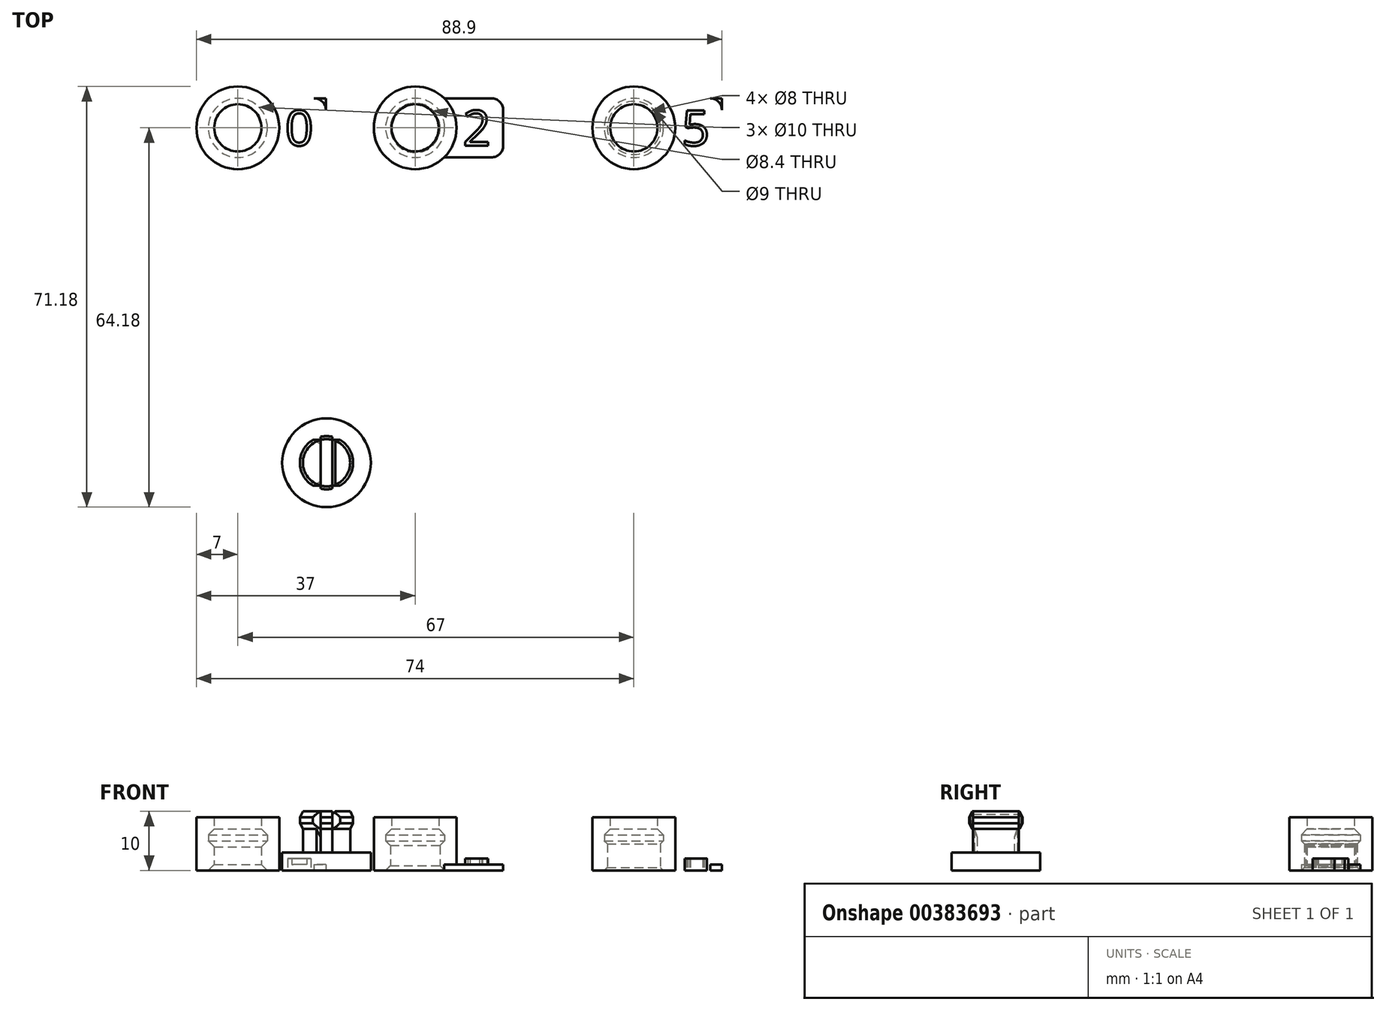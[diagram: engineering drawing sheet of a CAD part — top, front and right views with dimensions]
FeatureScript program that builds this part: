
annotation { "Feature Type Name" : "Feature", "Feature Type Description" : "" }
export const myFeature = defineFeature(function(context is Context, id is Id, definition is map)
    precondition{}
    {
        {
            var Q0;
            Q0=qCreatedBy(makeId("Front.planeOp"),FACE);
            var sketch = newSketch(context, id + "F0", { "sketchPlane" : qUnion([Q0])});
            skLineSegment(sketch, "E0", {"start": v(0, 0) * mm, "end": v(0, 7) * mm, "construction": true});
            skLineSegment(sketch, "E1", {"start": v(0, 7) * mm, "end": v(0, 9) * mm, "construction": true});
            skLineSegment(sketch, "E2", {"start": v(0, 9) * mm, "end": v(-4, 9) * mm, "construction": true});
            skLineSegment(sketch, "E3", {"start": v(0, 0) * mm, "end": v(-4, 0) * mm, "construction": true});
            skLineSegment(sketch, "E4", {"start": v(-4, 9) * mm, "end": v(-4, 7) * mm});
            skLineSegment(sketch, "E5", {"start": v(-4, 7) * mm, "end": v(-5, 6) * mm});
            skLineSegment(sketch, "E6", {"start": v(-5, 6) * mm, "end": v(-5, 5) * mm});
            skLineSegment(sketch, "E7", {"start": v(-5, 5) * mm, "end": v(-4, 4) * mm});
            skLineSegment(sketch, "E8", {"start": v(-4, 4) * mm, "end": v(-4, 0) * mm});
            skLineSegment(sketch, "E9", {"start": v(-4, 0) * mm, "end": v(-7, 0) * mm});
            skLineSegment(sketch, "E10", {"start": v(-7, 0) * mm, "end": v(-7, 9) * mm});
            skLineSegment(sketch, "E11", {"start": v(-7, 9) * mm, "end": v(-4, 9) * mm});
            skLineSegment(sketch, "E12", {"start": v(-4, 1) * mm, "end": v(-5, 0) * mm});
            skLineSegment(sketch, "E13", {"start": v(30, 0) * mm, "end": v(30, 7) * mm, "construction": true});
            skLineSegment(sketch, "E14", {"start": v(30, 7) * mm, "end": v(30, 9) * mm, "construction": true});
            skLineSegment(sketch, "E15", {"start": v(30, 9) * mm, "end": v(26, 9) * mm, "construction": true});
            skLineSegment(sketch, "E16", {"start": v(30, 0) * mm, "end": v(25.8, 0) * mm, "construction": true});
            skLineSegment(sketch, "E17", {"start": v(26, 9) * mm, "end": v(26, 7) * mm});
            skLineSegment(sketch, "E18", {"start": v(26, 7) * mm, "end": v(25, 6) * mm});
            skLineSegment(sketch, "E19", {"start": v(25, 6) * mm, "end": v(25, 5) * mm});
            skLineSegment(sketch, "E20", {"start": v(25, 5) * mm, "end": v(25.8, 4.2) * mm});
            skLineSegment(sketch, "E21", {"start": v(25.8, 4.2) * mm, "end": v(25.8, 0) * mm});
            skLineSegment(sketch, "E22", {"start": v(25.8, 0) * mm, "end": v(23, 0) * mm});
            skLineSegment(sketch, "E23", {"start": v(23, 0) * mm, "end": v(23, 9) * mm});
            skLineSegment(sketch, "E24", {"start": v(23, 9) * mm, "end": v(26, 9) * mm});
            skLineSegment(sketch, "E25", {"start": v(25.8, 0.8) * mm, "end": v(25, 0) * mm});
            skLineSegment(sketch, "E26", {"start": v(67, 0) * mm, "end": v(67, 7) * mm, "construction": true});
            skLineSegment(sketch, "E27", {"start": v(67, 7) * mm, "end": v(67, 9) * mm, "construction": true});
            skLineSegment(sketch, "E28", {"start": v(67, 9) * mm, "end": v(63, 9) * mm, "construction": true});
            skLineSegment(sketch, "E29", {"start": v(67, 0) * mm, "end": v(62.5, 0) * mm, "construction": true});
            skLineSegment(sketch, "E30", {"start": v(63, 9) * mm, "end": v(63, 7) * mm});
            skLineSegment(sketch, "E31", {"start": v(63, 7) * mm, "end": v(62, 6) * mm});
            skLineSegment(sketch, "E32", {"start": v(62, 6) * mm, "end": v(62, 5) * mm});
            skLineSegment(sketch, "E33", {"start": v(62, 5) * mm, "end": v(62.5, 4.5) * mm});
            skLineSegment(sketch, "E34", {"start": v(62.5, 4.5) * mm, "end": v(62.5, 0) * mm});
            skLineSegment(sketch, "E35", {"start": v(62.5, 0) * mm, "end": v(60, 0) * mm});
            skLineSegment(sketch, "E36", {"start": v(60, 0) * mm, "end": v(60, 9) * mm});
            skLineSegment(sketch, "E37", {"start": v(60, 9) * mm, "end": v(63, 9) * mm});
            skLineSegment(sketch, "E38", {"start": v(62.5, 0.5) * mm, "end": v(62, 0) * mm});
            skSolve(sketch);
        }
        {
            var Q0;
            Q0=makeQuery(id+"F0.imprint","IMPRINT",FACE,{"disambiguationData":[TD([[makeQuery(id+"F0.imprint","IMPRINT",EDGE,{"derivedFrom":sQuery(id+"F0.wireOp",EDGE,"E4")}),-1.0]])]});
            var Q1;
            Q1=sQuery(id+"F0.wireOp",EDGE,"E0");
            revolve(context, id + "F1", {"entities" : qUnion([Q0]), "axis" : qUnion([Q1]), "revolveType" : RevolveType.FULL});
        }
        {
            var Q0;
            Q0=makeQuery(id+"F0.imprint","IMPRINT",FACE,{"disambiguationData":[TD([[makeQuery(id+"F0.imprint","IMPRINT",EDGE,{"derivedFrom":sQuery(id+"F0.wireOp",EDGE,"E17")}),-1.0]])]});
            var Q1;
            Q1=sQuery(id+"F0.wireOp",EDGE,"E13");
            revolve(context, id + "F2", {"entities" : qUnion([Q0]), "axis" : qUnion([Q1]), "revolveType" : RevolveType.FULL});
        }
        {
            var Q0;
            Q0=makeQuery(id+"F0.imprint","IMPRINT",FACE,{"disambiguationData":[TD([[makeQuery(id+"F0.imprint","IMPRINT",EDGE,{"derivedFrom":sQuery(id+"F0.wireOp",EDGE,"E30")}),-1.0]])]});
            var Q1;
            Q1=sQuery(id+"F0.wireOp",EDGE,"E26");
            revolve(context, id + "F3", {"entities" : qUnion([Q0]), "axis" : qUnion([Q1]), "revolveType" : RevolveType.FULL});
        }
        {
            var Q0;
            Q0=qCreatedBy(makeId("Top.planeOp"),FACE);
            var sketch = newSketch(context, id + "F4", { "sketchPlane" : qUnion([Q0])});
            skCircle(sketch, "E39.0", {"center": v(0, 0) * mm, "radius": 7 * mm});
            skCircle(sketch, "E40.0", {"center": v(30, 0) * mm, "radius": 7 * mm});
            skCircle(sketch, "E41.0", {"center": v(67, 0) * mm, "radius": 7 * mm});
            skLineSegment(sketch, "E42.bottom", {"start": v(4.9, 5) * mm, "end": v(14.9, 5) * mm});
            skLineSegment(sketch, "E42.top", {"start": v(4.9, -5) * mm, "end": v(14.9, -5) * mm});
            skLineSegment(sketch, "E42.left", {"start": v(4.9, 5) * mm, "end": v(4.9, -5) * mm, "construction": true});
            skLineSegment(sketch, "E42.right", {"start": v(14.9, 5) * mm, "end": v(14.9, -5) * mm});
            skLineSegment(sketch, "E43", {"start": v(0, 0) * mm, "end": v(67, 0) * mm, "construction": true});
            skLineSegment(sketch, "E44.bottom", {"start": v(34.9, 5) * mm, "end": v(44.9, 5) * mm});
            skLineSegment(sketch, "E44.top", {"start": v(34.9, -5) * mm, "end": v(44.9, -5) * mm});
            skLineSegment(sketch, "E44.left", {"start": v(34.9, 5) * mm, "end": v(34.9, -5) * mm, "construction": true});
            skLineSegment(sketch, "E44.right", {"start": v(44.9, 5) * mm, "end": v(44.9, -5) * mm});
            skLineSegment(sketch, "E45.bottom", {"start": v(71.9, 5) * mm, "end": v(81.9, 5) * mm});
            skLineSegment(sketch, "E45.top", {"start": v(71.9, -5) * mm, "end": v(81.9, -5) * mm});
            skLineSegment(sketch, "E45.left", {"start": v(71.9, 5) * mm, "end": v(71.9, -5) * mm, "construction": true});
            skLineSegment(sketch, "E45.right", {"start": v(81.9, 5) * mm, "end": v(81.9, -5) * mm});
            skArc(sketch, "E46", {"start": v(12.9, 5) * mm, "mid": v(14.31, 4.41) * mm, "end": v(14.9, 3) * mm});
            skArc(sketch, "E47", {"start": v(14.9, -3) * mm, "mid": v(14.31, -4.41) * mm, "end": v(12.9, -5) * mm});
            skArc(sketch, "E48", {"start": v(42.9, -5) * mm, "mid": v(44.31, -4.41) * mm, "end": v(44.9, -3) * mm});
            skArc(sketch, "E49", {"start": v(42.9, 5) * mm, "mid": v(44.31, 4.41) * mm, "end": v(44.9, 3) * mm});
            skArc(sketch, "E50", {"start": v(79.9, 5) * mm, "mid": v(81.31, 4.41) * mm, "end": v(81.9, 3) * mm});
            skArc(sketch, "E51", {"start": v(81.9, -3) * mm, "mid": v(81.31, -4.41) * mm, "end": v(79.9, -5) * mm});
            skText(sketch, "E52", { "text": "0", "fontName": "OpenSans-Regular.ttf"});
            skText(sketch, "E53", { "text": "2", "fontName": "OpenSans-Regular.ttf"});
            skText(sketch, "E54", { "text": "5", "fontName": "OpenSans-Regular.ttf"});
            const initialGuessF4  = {"E52": [0.008, -0.003, 1, 0, 0.006], "E53": [0.03804, -0.003, 1, 0, 0.006], "E54": [0.07507, -0.003, 1, 0, 0.006]};
            skSetInitialGuess(sketch, initialGuessF4);
            skSolve(sketch);
        }
        {
            var Q0;
            {var subQ6=sQuery(id+"F4.wireOp",EDGE,"E46");Q0=makeQuery(id+"F4.imprint","IMPRINT",FACE,{"disambiguationData":[TD([[makeQuery(id+"F4.imprint","IMPRINT",EDGE,{"derivedFrom":subQ6}),-1.0]])]});}
            var Q1;
            Q1=makeQuery(id+"F4.imprint","IMPRINT",FACE,{"disambiguationData":[TD([[makeQuery(id+"F4.imprint","IMPRINT",EDGE,{"derivedFrom":sQuery(id+"F4.wireOp",EDGE,"E52.sketch_text.stroke-0")}),-1.0]])]});
            var Q2;
            Q2=makeQuery(id+"F4.imprint","IMPRINT",FACE,{"disambiguationData":[TD([[makeQuery(id+"F4.imprint","IMPRINT",EDGE,{"derivedFrom":sQuery(id+"F4.wireOp",EDGE,"E52.sketch_text.stroke-8")}),1.0]])]});
            extrude(context, id + "F5", {"entities" : qUnion([Q0, Q1, Q2]), "operationType" : NewBodyOperationType.ADD, "depth" : 1 * mm});
        }
        {
            var Q0;
            {var subQ3=sQuery(id+"F4.wireOp",EDGE,"E48");Q0=makeQuery(id+"F4.imprint","IMPRINT",FACE,{"disambiguationData":[TD([[makeQuery(id+"F4.imprint","IMPRINT",EDGE,{"derivedFrom":subQ3}),1.0]])]});}
            var Q1;
            Q1=makeQuery(id+"F4.imprint","IMPRINT",FACE,{"disambiguationData":[TD([[makeQuery(id+"F4.imprint","IMPRINT",EDGE,{"derivedFrom":sQuery(id+"F4.wireOp",EDGE,"E53.sketch_text.stroke-0")}),-1.0]])]});
            extrude(context, id + "F6", {"entities" : qUnion([Q0, Q1]), "operationType" : NewBodyOperationType.ADD, "depth" : 1 * mm});
        }
        {
            var Q0;
            {var subQ0=sQuery(id+"F4.wireOp",EDGE,"E50");Q0=makeQuery(id+"F4.imprint","IMPRINT",FACE,{"disambiguationData":[TD([[makeQuery(id+"F4.imprint","IMPRINT",EDGE,{"derivedFrom":subQ0}),-1.0]])]});}
            var Q1;
            Q1=makeQuery(id+"F4.imprint","IMPRINT",FACE,{"disambiguationData":[TD([[makeQuery(id+"F4.imprint","IMPRINT",EDGE,{"derivedFrom":sQuery(id+"F4.wireOp",EDGE,"E54.sketch_text.stroke-0")}),-1.0]])]});
            extrude(context, id + "F7", {"entities" : qUnion([Q0, Q1]), "operationType" : NewBodyOperationType.ADD, "depth" : 1 * mm});
        }
        {
            var Q0;
            Q0=makeQuery(id+"F4.imprint","IMPRINT",FACE,{"disambiguationData":[TD([[makeQuery(id+"F4.imprint","IMPRINT",EDGE,{"derivedFrom":sQuery(id+"F4.wireOp",EDGE,"E52.sketch_text.stroke-0")}),-1.0]])]});
            extrude(context, id + "F8", {"entities" : qUnion([Q0]), "operationType" : NewBodyOperationType.ADD, "depth" : 2 * mm});
        }
        {
            var Q0;
            Q0=makeQuery(id+"F4.imprint","IMPRINT",FACE,{"disambiguationData":[TD([[makeQuery(id+"F4.imprint","IMPRINT",EDGE,{"derivedFrom":sQuery(id+"F4.wireOp",EDGE,"E53.sketch_text.stroke-0")}),-1.0]])]});
            extrude(context, id + "F9", {"entities" : qUnion([Q0]), "operationType" : NewBodyOperationType.ADD, "depth" : 2 * mm});
        }
        {
            var Q0;
            Q0=makeQuery(id+"F4.imprint","IMPRINT",FACE,{"disambiguationData":[TD([[makeQuery(id+"F4.imprint","IMPRINT",EDGE,{"derivedFrom":sQuery(id+"F4.wireOp",EDGE,"E54.sketch_text.stroke-0")}),-1.0]])]});
            extrude(context, id + "F10", {"entities" : qUnion([Q0]), "operationType" : NewBodyOperationType.ADD, "depth" : 2 * mm});
        }
        {
            var Q0;
            Q0=qCreatedBy(makeId("Top.planeOp"),FACE);
            var sketch = newSketch(context, id + "F11", { "sketchPlane" : qUnion([Q0])});
            skLineSegment(sketch, "E55", {"start": v(0, -30.7) * mm, "end": v(30, -30.7) * mm, "construction": true});
            skLineSegment(sketch, "E56", {"start": v(30, -30.7) * mm, "end": v(15, -56.68) * mm, "construction": true});
            skLineSegment(sketch, "E57", {"start": v(15, -56.68) * mm, "end": v(0, -30.7) * mm, "construction": true});
            skLineSegment(sketch, "E58", {"start": v(0, -56.68) * mm, "end": v(30, -56.68) * mm, "construction": true});
            skLineSegment(sketch, "E59", {"start": v(15, -30.7) * mm, "end": v(15, -82.66) * mm, "construction": true});
            skSolve(sketch);
        }
        {
            var Q0;
            Q0=sQuery(id+"F11.wireOp",EDGE,"E58");
            cPoint(context, id + "F12", {"entities" : qUnion([Q0]), "parameter" : 0.5});
        }
        {
            var Q0;
            Q0=qCreatedBy(id+"F12",VERTEX);
            var Q1;
            Q1=sQuery(id+"F11.wireOp",EDGE,"E58");
            cPlane(context, id + "F13", {"entities" : qUnion([Q0, Q1]), "cplaneType" : CPlaneType.LINE_POINT, "offset" : 25 * mm, "width" : 150 * mm, "height" : 150 * mm});
        }
        {
            var Q0;
            Q0=qCreatedBy(id+"F13.planeOp",FACE);
            var sketch = newSketch(context, id + "F14", { "sketchPlane" : qUnion([Q0])});
            skPoint(sketch, "E60.0", {"position": v(-56.68, 0) * mm});
            skLineSegment(sketch, "E61", {"start": v(-56.68, 0) * mm, "end": v(-56.68, 10) * mm});
            skLineSegment(sketch, "E62", {"start": v(-56.68, 10) * mm, "end": v(-52.68, 10) * mm});
            skLineSegment(sketch, "E63", {"start": v(-52.68, 10) * mm, "end": v(-52.18, 9) * mm});
            skLineSegment(sketch, "E64", {"start": v(-52.18, 9) * mm, "end": v(-52.18, 8) * mm});
            skLineSegment(sketch, "E65", {"start": v(-52.18, 8) * mm, "end": v(-52.68, 7) * mm});
            skLineSegment(sketch, "E66", {"start": v(-52.68, 7) * mm, "end": v(-52.68, 0) * mm});
            skLineSegment(sketch, "E67", {"start": v(-52.68, 0) * mm, "end": v(-56.68, 0) * mm});
            skLineSegment(sketch, "E68", {"start": v(-52.68, 0) * mm, "end": v(-49.18, 0) * mm});
            skLineSegment(sketch, "E69", {"start": v(-49.18, 0) * mm, "end": v(-49.18, 3) * mm});
            skLineSegment(sketch, "E70", {"start": v(-49.18, 3) * mm, "end": v(-52.68, 3) * mm});
            skSolve(sketch);
        }
        {
            var Q0;
            {var subQ0=sQuery(id+"F14.wireOp",EDGE,"E68");Q0=makeQuery(id+"F14.imprint","IMPRINT",FACE,{"disambiguationData":[TD([[makeQuery(id+"F14.imprint","IMPRINT",EDGE,{"derivedFrom":subQ0}),1.0]])]});}
            var Q1;
            Q1=makeQuery(id+"F14.imprint","IMPRINT",FACE,{"disambiguationData":[TD([[makeQuery(id+"F14.imprint","IMPRINT",EDGE,{"derivedFrom":sQuery(id+"F14.wireOp",EDGE,"E61")}),-1.0]])]});
            var Q2;
            Q2=sQuery(id+"F14.wireOp",EDGE,"E61");
            revolve(context, id + "F15", {"entities" : qUnion([Q0, Q1]), "axis" : qUnion([Q2]), "revolveType" : RevolveType.FULL});
        }
        {
            var Q0;
            Q0=makeQuery(id+"F15.opRevolve","SWEPT_FACE",FACE,{"disambiguationData":[OSD([sQuery(id+"F14.wireOp",EDGE,"E62")])]});
            var sketch = newSketch(context, id + "F16", { "sketchPlane" : qUnion([Q0])});
            skCircle(sketch, "E71.0", {"center": v(15, -56.68) * mm, "radius": 4.5 * mm, "construction": true});
            skCircle(sketch, "E72.0", {"center": v(15, -56.68) * mm, "radius": 4 * mm, "construction": true});
            skLineSegment(sketch, "E73.bottom", {"start": v(14, -52.18) * mm, "end": v(16, -52.18) * mm});
            skLineSegment(sketch, "E73.top", {"start": v(14, -61.18) * mm, "end": v(16, -61.18) * mm});
            skLineSegment(sketch, "E73.left", {"start": v(14, -52.18) * mm, "end": v(14, -61.18) * mm});
            skLineSegment(sketch, "E73.right", {"start": v(16, -52.18) * mm, "end": v(16, -61.18) * mm});
            skLineSegment(sketch, "E74", {"start": v(14, -61.18) * mm, "end": v(16, -52.18) * mm, "construction": true});
            skLineSegment(sketch, "E75.bottom", {"start": v(12.7, -61.18) * mm, "end": v(17.3, -61.18) * mm});
            skLineSegment(sketch, "E75.top", {"start": v(12.7, -60.55) * mm, "end": v(17.3, -60.55) * mm});
            skLineSegment(sketch, "E75.left", {"start": v(12.7, -60.55) * mm, "end": v(12.7, -61.18) * mm});
            skLineSegment(sketch, "E75.right", {"start": v(17.3, -60.55) * mm, "end": v(17.3, -61.18) * mm});
            skPoint(sketch, "E76", {"position": v(15, -61.18) * mm});
            skLineSegment(sketch, "E77.bottom", {"start": v(12.7, -52.18) * mm, "end": v(17.3, -52.18) * mm});
            skLineSegment(sketch, "E77.top", {"start": v(12.7, -52.8) * mm, "end": v(17.3, -52.8) * mm});
            skLineSegment(sketch, "E77.left", {"start": v(12.7, -52.18) * mm, "end": v(12.7, -52.8) * mm});
            skLineSegment(sketch, "E77.right", {"start": v(17.3, -52.18) * mm, "end": v(17.3, -52.8) * mm});
            skPoint(sketch, "E78", {"position": v(15, -52.18) * mm});
            skPoint(sketch, "E79", {"position": v(16, -60.55) * mm});
            skPoint(sketch, "E80", {"position": v(16, -52.8) * mm});
            skSolve(sketch);
        }
        {
            var Q0;
            {var subQ5=sQuery(id+"F16.wireOp",EDGE,"E77.left");Q0=makeQuery(id+"F16.imprint","IMPRINT",FACE,{"disambiguationData":[TD([[makeQuery(id+"F16.imprint","IMPRINT",EDGE,{"derivedFrom":subQ5}),1.0]])]});}
            var Q1;
            {var subQ0=sQuery(id+"F16.wireOp",EDGE,"E77.bottom");var subQ1=sQuery(id+"F16.wireOp",EDGE,"E73.left");var subQ2=makeQuery(id+"F16.imprint","INTERSECT",VERTEX,{"derivedFrom":[subQ1,subQ0]});Q1=makeQuery(id+"F16.imprint","IMPRINT",FACE,{"disambiguationData":[TD([[makeQuery(id+"F16.imprint","IMPRINT",EDGE,{"disambiguationData":[TD([[subQ2,-1.0]])],"derivedFrom":subQ0}),-1.0]])]});}
            var Q2;
            {var subQ5=sQuery(id+"F16.wireOp",EDGE,"E77.right");Q2=makeQuery(id+"F16.imprint","IMPRINT",FACE,{"disambiguationData":[TD([[makeQuery(id+"F16.imprint","IMPRINT",EDGE,{"derivedFrom":subQ5}),-1.0]])]});}
            var Q3;
            {var subQ0=sQuery(id+"F16.wireOp",EDGE,"E77.top");var subQ1=makeQuery(id+"F15.opRevolve","SWEPT_EDGE",EDGE,{"disambiguationData":[OSD([sQuery(id+"F14.wireOp",EDGE,"E62"),sQuery(id+"F14.wireOp",EDGE,"E63")])]});var subQ2=makeQuery(id+"F16.imprint","INTERSECT",VERTEX,{"derivedFrom":[subQ1,sQuery(id+"F16.wireOp",EDGE,"E73.left"),subQ0]});Q3=makeQuery(id+"F16.imprint","IMPRINT",FACE,{"disambiguationData":[TD([[makeQuery(id+"F16.imprint","IMPRINT",EDGE,{"disambiguationData":[TD([[subQ2,-1.0]])],"derivedFrom":subQ0}),1.0]])]});}
            var Q4;
            {var subQ0=sQuery(id+"F16.wireOp",EDGE,"E77.top");var subQ1=sQuery(id+"F16.wireOp",EDGE,"E73.left");var subQ2=makeQuery(id+"F15.opRevolve","SWEPT_EDGE",EDGE,{"disambiguationData":[OSD([sQuery(id+"F14.wireOp",EDGE,"E62"),sQuery(id+"F14.wireOp",EDGE,"E63")])]});var subQ3=makeQuery(id+"F16.imprint","INTERSECT",VERTEX,{"derivedFrom":[subQ2,subQ1,subQ0]});Q4=makeQuery(id+"F16.imprint","IMPRINT",FACE,{"disambiguationData":[TD([[makeQuery(id+"F16.imprint","IMPRINT",EDGE,{"disambiguationData":[TD([[subQ3,-1.0]])],"derivedFrom":subQ1}),1.0]])]});}
            var Q5;
            {var subQ0=sQuery(id+"F16.wireOp",EDGE,"E75.top");var subQ1=makeQuery(id+"F15.opRevolve","SWEPT_EDGE",EDGE,{"disambiguationData":[OSD([sQuery(id+"F14.wireOp",EDGE,"E62"),sQuery(id+"F14.wireOp",EDGE,"E63")])]});var subQ2=makeQuery(id+"F16.imprint","INTERSECT",VERTEX,{"derivedFrom":[subQ1,sQuery(id+"F16.wireOp",EDGE,"E73.left"),subQ0]});Q5=makeQuery(id+"F16.imprint","IMPRINT",FACE,{"disambiguationData":[TD([[makeQuery(id+"F16.imprint","IMPRINT",EDGE,{"disambiguationData":[TD([[subQ2,-1.0]])],"derivedFrom":subQ0}),-1.0]])]});}
            var Q6;
            {var subQ5=sQuery(id+"F16.wireOp",EDGE,"E75.right");Q6=makeQuery(id+"F16.imprint","IMPRINT",FACE,{"disambiguationData":[TD([[makeQuery(id+"F16.imprint","IMPRINT",EDGE,{"derivedFrom":subQ5}),-1.0]])]});}
            var Q7;
            {var subQ0=sQuery(id+"F16.wireOp",EDGE,"E75.bottom");var subQ1=sQuery(id+"F16.wireOp",EDGE,"E73.left");var subQ2=makeQuery(id+"F16.imprint","INTERSECT",VERTEX,{"derivedFrom":[subQ1,subQ0]});Q7=makeQuery(id+"F16.imprint","IMPRINT",FACE,{"disambiguationData":[TD([[makeQuery(id+"F16.imprint","IMPRINT",EDGE,{"disambiguationData":[TD([[subQ2,-1.0]])],"derivedFrom":subQ0}),1.0]])]});}
            var Q8;
            {var subQ5=sQuery(id+"F16.wireOp",EDGE,"E75.left");Q8=makeQuery(id+"F16.imprint","IMPRINT",FACE,{"disambiguationData":[TD([[makeQuery(id+"F16.imprint","IMPRINT",EDGE,{"derivedFrom":subQ5}),1.0]])]});}
            var Q9;
            Q9=makeQuery(id+"F15.opRevolve","SWEPT_FACE",FACE,{"disambiguationData":[OSD([sQuery(id+"F14.wireOp",EDGE,"E70")])]});
            extrude(context, id + "F17", {"entities" : qUnion([Q0, Q1, Q2, Q3, Q4, Q5, Q6, Q7, Q8]), "operationType" : NewBodyOperationType.REMOVE, "endBound" : BoundingType.UP_TO_SURFACE, "oppositeDirection" : true, "endBoundEntityFace" : qUnion([Q9]), "depth" : 25 * mm});
        }
        {
            var Q0;
            {var subQ0=sQuery(id+"F14.wireOp",EDGE,"E63");var subQ1=sQuery(id+"F14.wireOp",EDGE,"E62");var subQ2=sQuery(id+"F16.wireOp",EDGE,"E73.left");var subQ3=sQuery(id+"F16.wireOp",EDGE,"E75.top");Q0=makeQuery(id+"F17.boolean.opBoolean","COPY",EDGE,{"disambiguationData":[TD([makeQuery(id+"F15.opRevolve","SWEPT_FACE",FACE,{"disambiguationData":[OSD([subQ1])]})])],"derivedFrom":makeQuery(id+"F17.opExtrude","SWEPT_EDGE",EDGE,{"disambiguationData":[OSD([subQ1,subQ0,subQ2,subQ3])]})});}
            var Q1;
            Q1=makeQuery(id+"F17.boolean.opBoolean","COPY",EDGE,{"derivedFrom":makeQuery(id+"F17.opExtrude","CAP_EDGE",EDGE,{"disambiguationData":[OSD([sQuery(id+"F16.wireOp",EDGE,"E73.left")])],"isStart":true})});
            var Q2;
            {var subQ0=sQuery(id+"F16.wireOp",EDGE,"E75.top");var subQ1=sQuery(id+"F16.wireOp",EDGE,"E73.right");var subQ2=sQuery(id+"F14.wireOp",EDGE,"E63");var subQ3=sQuery(id+"F14.wireOp",EDGE,"E62");Q2=makeQuery(id+"F17.boolean.opBoolean","COPY",EDGE,{"disambiguationData":[TD([makeQuery(id+"F15.opRevolve","SWEPT_FACE",FACE,{"disambiguationData":[OSD([subQ3])]})])],"derivedFrom":makeQuery(id+"F17.opExtrude","SWEPT_EDGE",EDGE,{"disambiguationData":[OSD([subQ3,subQ2,subQ1,subQ0])]})});}
            var Q3;
            Q3=makeQuery(id+"F17.boolean.opBoolean","COPY",EDGE,{"derivedFrom":makeQuery(id+"F17.opExtrude","CAP_EDGE",EDGE,{"disambiguationData":[OSD([sQuery(id+"F16.wireOp",EDGE,"E73.right")])],"isStart":true})});
            var Q4;
            {var subQ0=sQuery(id+"F14.wireOp",EDGE,"E63");var subQ1=sQuery(id+"F14.wireOp",EDGE,"E62");var subQ2=sQuery(id+"F16.wireOp",EDGE,"E73.left");var subQ3=sQuery(id+"F16.wireOp",EDGE,"E77.top");Q4=makeQuery(id+"F17.boolean.opBoolean","COPY",EDGE,{"disambiguationData":[TD([makeQuery(id+"F15.opRevolve","SWEPT_FACE",FACE,{"disambiguationData":[OSD([subQ1])]})])],"derivedFrom":makeQuery(id+"F17.opExtrude","SWEPT_EDGE",EDGE,{"disambiguationData":[OSD([subQ1,subQ0,subQ2,subQ3])]})});}
            var Q5;
            {var subQ0=sQuery(id+"F14.wireOp",EDGE,"E63");var subQ1=sQuery(id+"F14.wireOp",EDGE,"E62");var subQ2=sQuery(id+"F16.wireOp",EDGE,"E73.right");var subQ3=sQuery(id+"F16.wireOp",EDGE,"E77.top");Q5=makeQuery(id+"F17.boolean.opBoolean","COPY",EDGE,{"disambiguationData":[TD([makeQuery(id+"F15.opRevolve","SWEPT_FACE",FACE,{"disambiguationData":[OSD([subQ1])]})])],"derivedFrom":makeQuery(id+"F17.opExtrude","SWEPT_EDGE",EDGE,{"disambiguationData":[OSD([subQ1,subQ0,subQ2,subQ3])]})});}
            chamfer(context, id + "F18", {"entities" : qUnion([Q0, Q1, Q2, Q3, Q4, Q5]), "width" : .5 * mm, "tangentPropagation" : true});
        }
    });
